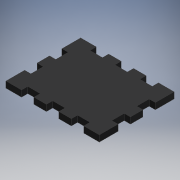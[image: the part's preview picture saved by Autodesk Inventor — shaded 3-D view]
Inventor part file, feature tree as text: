
AUTODESK INVENTOR PART (.ipt)
format: ipt  version: 2019 (Build 230136000, 136)  size: 169,984 bytes
history: native  units: mm
features: extrude x2, sketch x2, projected_geometry x1
ambient origin geometry x8: Origin, YZ Plane, XZ Plane, XY Plane, X Axis, Y Axis, Z Axis, Center Point
bodies: Solid1 (feature_tree)
feature tree (5):
  extrude  "Extrusion1"  Depth=48.0mm
  extrude  "Extrusion2"  Depth=4.0mm
  sketch  "Sketch1"  dims[d0=60.0mm d1=48.0mm]
  sketch  "Sketch2"  dims[d2=4.0mm d3=0.0mm d4=4.0mm d7=8.0mm d8=8.0mm d9=4.0mm d10=8.0mm d11=4.0mm d12=4.0mm d13=0.0mm]
  projected_geometry  "Projected Loop1"
